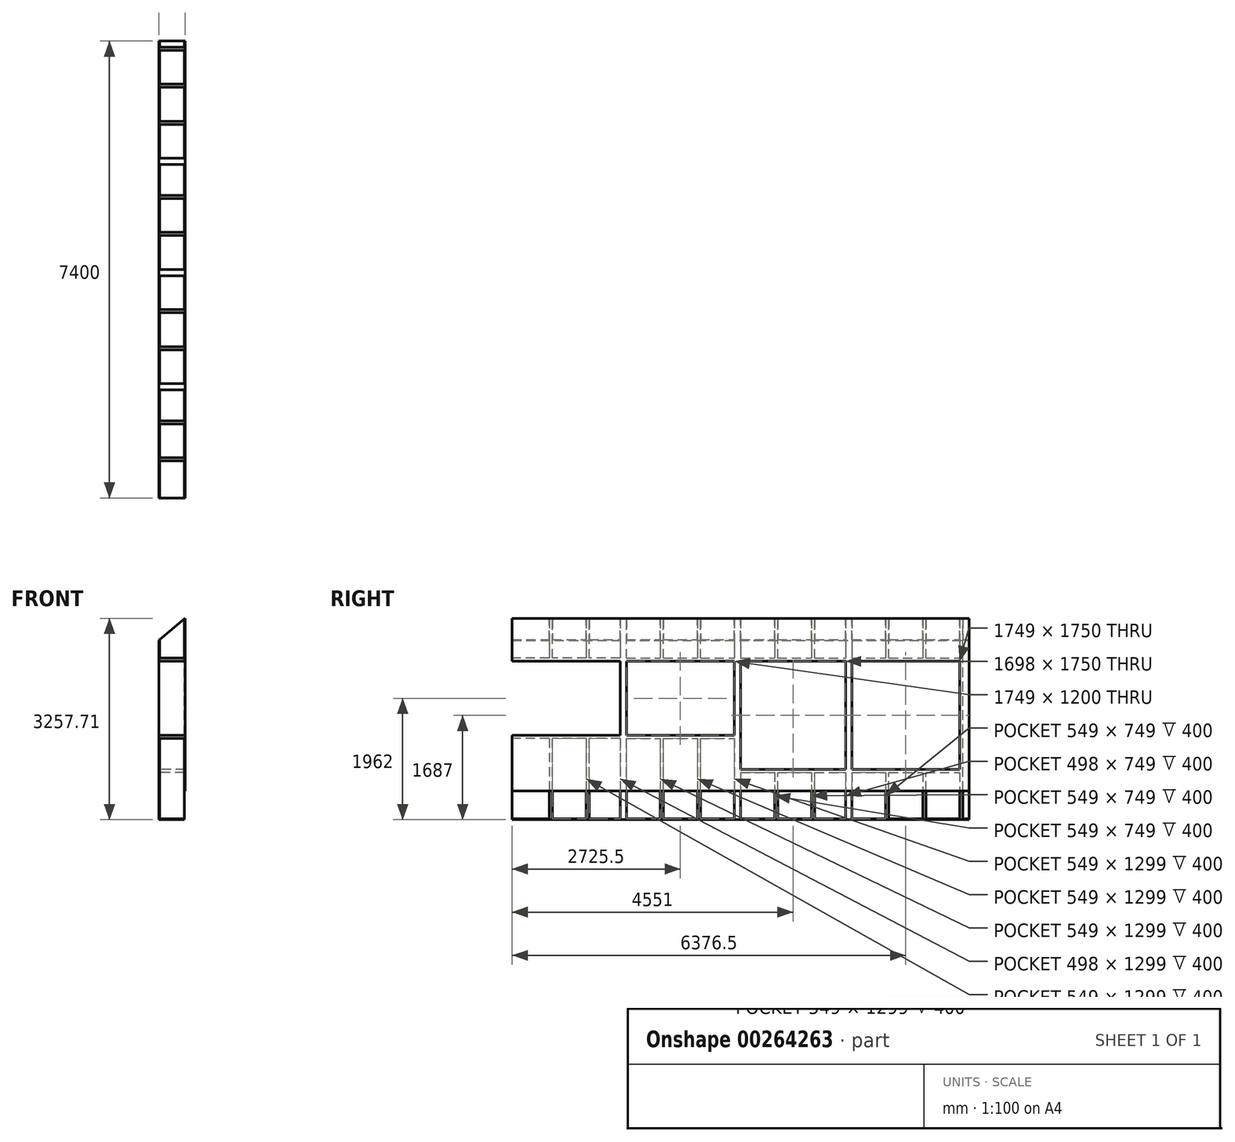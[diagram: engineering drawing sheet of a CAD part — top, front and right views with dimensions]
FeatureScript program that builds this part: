
annotation { "Feature Type Name" : "Feature", "Feature Type Description" : "" }
export const myFeature = defineFeature(function(context is Context, id is Id, definition is map)
    precondition{}
    {
        {
            var Q0;
            Q0=qCreatedBy(makeId("Right.planeOp"),FACE);
            var sketch = newSketch(context, id + "F0", { "sketchPlane" : qUnion([Q0])});
            skLineSegment(sketch, "E0.bottom", {"start": v(0, 0) * mm, "end": v(-7400, 0) * mm});
            skLineSegment(sketch, "E0.top", {"start": v(0, 3300) * mm, "end": v(-7400, 3300) * mm});
            skLineSegment(sketch, "E0.left", {"start": v(0, 0) * mm, "end": v(0, 3300) * mm});
            skLineSegment(sketch, "E0.right", {"start": v(-7400, 0) * mm, "end": v(-7400, 3300) * mm});
            skLineSegment(sketch, "E1", {"start": v(-6800, 3300) * mm, "end": v(-6800, 2601) * mm});
            skLineSegment(sketch, "E2", {"start": v(-6749, 0) * mm, "end": v(-6749, 1299) * mm});
            skLineSegment(sketch, "E3.1.0.0", {"start": v(-6149, 0) * mm, "end": v(-6149, 1299) * mm});
            skLineSegment(sketch, "E3.1.0.1", {"start": v(-6200, 3300) * mm, "end": v(-6200, 2601) * mm});
            skLineSegment(sketch, "E3.2.0.0", {"start": v(-5549, 0) * mm, "end": v(-5549, 3300) * mm});
            skLineSegment(sketch, "E3.2.0.1", {"start": v(-5600, 3300) * mm, "end": v(-5600, 0) * mm});
            skLineSegment(sketch, "E3.3.0.0", {"start": v(-4949, 0) * mm, "end": v(-4949, 1299) * mm});
            skLineSegment(sketch, "E3.3.0.1", {"start": v(-5000, 3300) * mm, "end": v(-5000, 2601) * mm});
            skLineSegment(sketch, "E3.4.0.0", {"start": v(-4349, 0) * mm, "end": v(-4349, 1299) * mm});
            skLineSegment(sketch, "E3.4.0.1", {"start": v(-4400, 3300) * mm, "end": v(-4400, 2601) * mm});
            skLineSegment(sketch, "E3.5.0.0", {"start": v(-3749, 0) * mm, "end": v(-3749, 3300) * mm});
            skLineSegment(sketch, "E3.5.0.1", {"start": v(-3800, 3300) * mm, "end": v(-3800, 0) * mm});
            skLineSegment(sketch, "E3.6.0.0", {"start": v(-3098, 0) * mm, "end": v(-3098, 749) * mm});
            skLineSegment(sketch, "E3.6.0.1", {"start": v(-3149, 3300) * mm, "end": v(-3149, 2601) * mm});
            skLineSegment(sketch, "E3.7.0.0", {"start": v(-2498, 0) * mm, "end": v(-2498, 749) * mm});
            skLineSegment(sketch, "E3.7.0.1", {"start": v(-2549, 3300) * mm, "end": v(-2549, 2601) * mm});
            skLineSegment(sketch, "E3.8.0.0", {"start": v(-1949, 0) * mm, "end": v(-1949, 3300) * mm});
            skLineSegment(sketch, "E3.8.0.1", {"start": v(-2000, 3300) * mm, "end": v(-2000, 0) * mm});
            skLineSegment(sketch, "E3.9.0.0", {"start": v(-1298, 0) * mm, "end": v(-1298, 749) * mm});
            skLineSegment(sketch, "E3.9.0.1", {"start": v(-1349, 3300) * mm, "end": v(-1349, 2601) * mm});
            skLineSegment(sketch, "E3.10.0.0", {"start": v(-698, 0) * mm, "end": v(-698, 749) * mm});
            skLineSegment(sketch, "E3.10.0.1", {"start": v(-749, 3300) * mm, "end": v(-749, 2601) * mm});
            skLineSegment(sketch, "E3.11.0.0", {"start": v(-98, 0) * mm, "end": v(-98, 3300) * mm});
            skLineSegment(sketch, "E3.11.0.1", {"start": v(-149, 3300) * mm, "end": v(-149, 0) * mm});
            skLineSegment(sketch, "E3.direction1", {"start": v(-6800, 0) * mm, "end": v(-6200, 0) * mm, "construction": true});
            skLineSegment(sketch, "E4", {"start": v(-7400, 1350) * mm, "end": v(-5651, 1350) * mm});
            skLineSegment(sketch, "E5", {"start": v(-5651, 3300) * mm, "end": v(-5651, 0) * mm});
            skLineSegment(sketch, "E6", {"start": v(-7400, 2550) * mm, "end": v(-5651, 2550) * mm});
            skLineSegment(sketch, "E7", {"start": v(-5651, 2601) * mm, "end": v(-7400, 2601) * mm});
            skLineSegment(sketch, "E8", {"start": v(-5651, 1299) * mm, "end": v(-7400, 1299) * mm});
            skLineSegment(sketch, "E9", {"start": v(-5549, 2601) * mm, "end": v(-3800, 2601) * mm});
            skLineSegment(sketch, "E10", {"start": v(-5549, 2550) * mm, "end": v(-3800, 2550) * mm});
            skLineSegment(sketch, "E11", {"start": v(-5549, 1350) * mm, "end": v(-3800, 1350) * mm});
            skLineSegment(sketch, "E12", {"start": v(-5549, 1299) * mm, "end": v(-3800, 1299) * mm});
            skLineSegment(sketch, "E13", {"start": v(-3698, 3300) * mm, "end": v(-3698, 0) * mm});
            skLineSegment(sketch, "E14.trimOffspring", {"start": v(-4349, 2601) * mm, "end": v(-4349, 3300) * mm});
            skLineSegment(sketch, "E15.trimOffspring", {"start": v(-4400, 1299) * mm, "end": v(-4400, 0) * mm});
            skLineSegment(sketch, "E16.trimOffspring", {"start": v(-4949, 2601) * mm, "end": v(-4949, 3300) * mm});
            skLineSegment(sketch, "E17.trimOffspring", {"start": v(-5000, 1299) * mm, "end": v(-5000, 0) * mm});
            skLineSegment(sketch, "E18.trimOffspring", {"start": v(-6149, 2601) * mm, "end": v(-6149, 3300) * mm});
            skLineSegment(sketch, "E19.trimOffspring", {"start": v(-6200, 1299) * mm, "end": v(-6200, 0) * mm});
            skLineSegment(sketch, "E20.trimOffspring", {"start": v(-6749, 2601) * mm, "end": v(-6749, 3300) * mm});
            skLineSegment(sketch, "E21.trimOffspring", {"start": v(-6800, 1299) * mm, "end": v(-6800, 0) * mm});
            skLineSegment(sketch, "E22", {"start": v(-3698, 2601) * mm, "end": v(-2000, 2601) * mm});
            skLineSegment(sketch, "E23", {"start": v(-3698, 2550) * mm, "end": v(-2000, 2550) * mm});
            skLineSegment(sketch, "E24", {"start": v(-3698, 749) * mm, "end": v(-2000, 749) * mm});
            skLineSegment(sketch, "E25", {"start": v(-3698, 800) * mm, "end": v(-2000, 800) * mm});
            skLineSegment(sketch, "E26.trimOffspring", {"start": v(-3149, 749) * mm, "end": v(-3149, 0) * mm});
            skLineSegment(sketch, "E27.trimOffspring", {"start": v(-3098, 2601) * mm, "end": v(-3098, 3300) * mm});
            skLineSegment(sketch, "E28.trimOffspring", {"start": v(-2549, 749) * mm, "end": v(-2549, 0) * mm});
            skLineSegment(sketch, "E29.trimOffspring", {"start": v(-2498, 2601) * mm, "end": v(-2498, 3300) * mm});
            skLineSegment(sketch, "E30", {"start": v(-1898, 3300) * mm, "end": v(-1898, 0) * mm});
            skLineSegment(sketch, "E31", {"start": v(-1898, 2601) * mm, "end": v(-149, 2601) * mm});
            skLineSegment(sketch, "E32", {"start": v(-1898, 2550) * mm, "end": v(-149, 2550) * mm});
            skLineSegment(sketch, "E33", {"start": v(-1898, 800) * mm, "end": v(-149, 800) * mm});
            skLineSegment(sketch, "E34", {"start": v(-1898, 749) * mm, "end": v(-149, 749) * mm});
            skLineSegment(sketch, "E35.trimOffspring", {"start": v(-1349, 749) * mm, "end": v(-1349, 0) * mm});
            skLineSegment(sketch, "E36.trimOffspring", {"start": v(-1298, 2601) * mm, "end": v(-1298, 3300) * mm});
            skLineSegment(sketch, "E37.trimOffspring", {"start": v(-749, 749) * mm, "end": v(-749, 0) * mm});
            skLineSegment(sketch, "E38.trimOffspring", {"start": v(-698, 2601) * mm, "end": v(-698, 3300) * mm});
            skSolve(sketch);
        }
        {
            var Q0;
            {var subQ0=sQuery(id+"F0.wireOp",EDGE,"E3.11.0.0");Q0=makeQuery(id+"F0.imprint","IMPRINT",FACE,{"disambiguationData":[TD([[makeQuery(id+"F0.imprint","IMPRINT",EDGE,{"derivedFrom":subQ0}),1.0]])]});}
            var Q1;
            {var subQ0=sQuery(id+"F0.wireOp",EDGE,"E3.9.0.0");Q1=makeQuery(id+"F0.imprint","IMPRINT",FACE,{"disambiguationData":[TD([[makeQuery(id+"F0.imprint","IMPRINT",EDGE,{"derivedFrom":subQ0}),1.0]])]});}
            var Q2;
            {var subQ0=sQuery(id+"F0.wireOp",EDGE,"E3.7.0.0");Q2=makeQuery(id+"F0.imprint","IMPRINT",FACE,{"disambiguationData":[TD([[makeQuery(id+"F0.imprint","IMPRINT",EDGE,{"derivedFrom":subQ0}),1.0]])]});}
            var Q3;
            {var subQ0=sQuery(id+"F0.wireOp",EDGE,"E3.6.0.0");Q3=makeQuery(id+"F0.imprint","IMPRINT",FACE,{"disambiguationData":[TD([[makeQuery(id+"F0.imprint","IMPRINT",EDGE,{"derivedFrom":subQ0}),1.0]])]});}
            var Q4;
            {var subQ0=sQuery(id+"F0.wireOp",EDGE,"E3.4.0.0");Q4=makeQuery(id+"F0.imprint","IMPRINT",FACE,{"disambiguationData":[TD([[makeQuery(id+"F0.imprint","IMPRINT",EDGE,{"derivedFrom":subQ0}),1.0]])]});}
            var Q5;
            {var subQ0=sQuery(id+"F0.wireOp",EDGE,"E3.3.0.0");Q5=makeQuery(id+"F0.imprint","IMPRINT",FACE,{"disambiguationData":[TD([[makeQuery(id+"F0.imprint","IMPRINT",EDGE,{"derivedFrom":subQ0}),1.0]])]});}
            var Q6;
            {var subQ0=sQuery(id+"F0.wireOp",EDGE,"E3.1.0.0");Q6=makeQuery(id+"F0.imprint","IMPRINT",FACE,{"disambiguationData":[TD([[makeQuery(id+"F0.imprint","IMPRINT",EDGE,{"derivedFrom":subQ0}),1.0]])]});}
            var Q7;
            {var subQ0=sQuery(id+"F0.wireOp",EDGE,"E2");Q7=makeQuery(id+"F0.imprint","IMPRINT",FACE,{"disambiguationData":[TD([[makeQuery(id+"F0.imprint","IMPRINT",EDGE,{"derivedFrom":subQ0}),1.0]])]});}
            var Q8;
            {var subQ0=sQuery(id+"F0.wireOp",EDGE,"E3.9.0.1");Q8=makeQuery(id+"F0.imprint","IMPRINT",FACE,{"disambiguationData":[TD([[makeQuery(id+"F0.imprint","IMPRINT",EDGE,{"derivedFrom":subQ0}),1.0]])]});}
            var Q9;
            {var subQ0=sQuery(id+"F0.wireOp",EDGE,"E3.7.0.1");Q9=makeQuery(id+"F0.imprint","IMPRINT",FACE,{"disambiguationData":[TD([[makeQuery(id+"F0.imprint","IMPRINT",EDGE,{"derivedFrom":subQ0}),1.0]])]});}
            var Q10;
            {var subQ0=sQuery(id+"F0.wireOp",EDGE,"E3.6.0.1");Q10=makeQuery(id+"F0.imprint","IMPRINT",FACE,{"disambiguationData":[TD([[makeQuery(id+"F0.imprint","IMPRINT",EDGE,{"derivedFrom":subQ0}),1.0]])]});}
            var Q11;
            {var subQ0=sQuery(id+"F0.wireOp",EDGE,"E3.4.0.1");Q11=makeQuery(id+"F0.imprint","IMPRINT",FACE,{"disambiguationData":[TD([[makeQuery(id+"F0.imprint","IMPRINT",EDGE,{"derivedFrom":subQ0}),1.0]])]});}
            var Q12;
            {var subQ0=sQuery(id+"F0.wireOp",EDGE,"E3.3.0.1");Q12=makeQuery(id+"F0.imprint","IMPRINT",FACE,{"disambiguationData":[TD([[makeQuery(id+"F0.imprint","IMPRINT",EDGE,{"derivedFrom":subQ0}),1.0]])]});}
            var Q13;
            {var subQ0=sQuery(id+"F0.wireOp",EDGE,"E3.1.0.1");Q13=makeQuery(id+"F0.imprint","IMPRINT",FACE,{"disambiguationData":[TD([[makeQuery(id+"F0.imprint","IMPRINT",EDGE,{"derivedFrom":subQ0}),1.0]])]});}
            var Q14;
            {var subQ0=sQuery(id+"F0.wireOp",EDGE,"E1");Q14=makeQuery(id+"F0.imprint","IMPRINT",FACE,{"disambiguationData":[TD([[makeQuery(id+"F0.imprint","IMPRINT",EDGE,{"derivedFrom":subQ0}),1.0]])]});}
            var Q15;
            {var subQ4=sQuery(id+"F0.wireOp",EDGE,"E3.10.0.0");Q15=makeQuery(id+"F0.imprint","IMPRINT",FACE,{"disambiguationData":[TD([[makeQuery(id+"F0.imprint","IMPRINT",EDGE,{"derivedFrom":subQ4}),1.0]])]});}
            var Q16;
            {var subQ0=sQuery(id+"F0.wireOp",EDGE,"E3.8.0.0");Q16=makeQuery(id+"F0.imprint","IMPRINT",FACE,{"disambiguationData":[TD([[makeQuery(id+"F0.imprint","IMPRINT",EDGE,{"derivedFrom":subQ0}),-1.0]])]});}
            var Q17;
            {var subQ4=sQuery(id+"F0.wireOp",EDGE,"E3.8.0.0");Q17=makeQuery(id+"F0.imprint","IMPRINT",FACE,{"disambiguationData":[TD([[makeQuery(id+"F0.imprint","IMPRINT",EDGE,{"derivedFrom":subQ4}),1.0]])]});}
            var Q18;
            {var subQ4=sQuery(id+"F0.wireOp",EDGE,"E3.5.0.0");Q18=makeQuery(id+"F0.imprint","IMPRINT",FACE,{"disambiguationData":[TD([[makeQuery(id+"F0.imprint","IMPRINT",EDGE,{"derivedFrom":subQ4}),-1.0]])]});}
            var Q19;
            {var subQ4=sQuery(id+"F0.wireOp",EDGE,"E3.5.0.0");Q19=makeQuery(id+"F0.imprint","IMPRINT",FACE,{"disambiguationData":[TD([[makeQuery(id+"F0.imprint","IMPRINT",EDGE,{"derivedFrom":subQ4}),1.0]])]});}
            var Q20;
            {var subQ5=sQuery(id+"F0.wireOp",EDGE,"E3.2.0.1");Q20=makeQuery(id+"F0.imprint","IMPRINT",FACE,{"disambiguationData":[TD([[makeQuery(id+"F0.imprint","IMPRINT",EDGE,{"derivedFrom":subQ5}),1.0]])]});}
            var Q21;
            {var subQ4=sQuery(id+"F0.wireOp",EDGE,"E3.2.0.1");Q21=makeQuery(id+"F0.imprint","IMPRINT",FACE,{"disambiguationData":[TD([[makeQuery(id+"F0.imprint","IMPRINT",EDGE,{"derivedFrom":subQ4}),-1.0]])]});}
            var Q22;
            {var subQ4=sQuery(id+"F0.wireOp",EDGE,"E4");Q22=makeQuery(id+"F0.imprint","IMPRINT",FACE,{"disambiguationData":[TD([[makeQuery(id+"F0.imprint","IMPRINT",EDGE,{"derivedFrom":subQ4}),-1.0]])]});}
            var Q23;
            {var subQ0=sQuery(id+"F0.wireOp",EDGE,"E6");Q23=makeQuery(id+"F0.imprint","IMPRINT",FACE,{"disambiguationData":[TD([[makeQuery(id+"F0.imprint","IMPRINT",EDGE,{"derivedFrom":subQ0}),1.0]])]});}
            var Q24;
            {var subQ4=sQuery(id+"F0.wireOp",EDGE,"E33");Q24=makeQuery(id+"F0.imprint","IMPRINT",FACE,{"disambiguationData":[TD([[makeQuery(id+"F0.imprint","IMPRINT",EDGE,{"derivedFrom":subQ4}),-1.0]])]});}
            var Q25;
            {var subQ5=sQuery(id+"F0.wireOp",EDGE,"E25");Q25=makeQuery(id+"F0.imprint","IMPRINT",FACE,{"disambiguationData":[TD([[makeQuery(id+"F0.imprint","IMPRINT",EDGE,{"derivedFrom":subQ5}),-1.0]])]});}
            var Q26;
            {var subQ4=sQuery(id+"F0.wireOp",EDGE,"E11");Q26=makeQuery(id+"F0.imprint","IMPRINT",FACE,{"disambiguationData":[TD([[makeQuery(id+"F0.imprint","IMPRINT",EDGE,{"derivedFrom":subQ4}),-1.0]])]});}
            var Q27;
            {var subQ5=sQuery(id+"F0.wireOp",EDGE,"E10");Q27=makeQuery(id+"F0.imprint","IMPRINT",FACE,{"disambiguationData":[TD([[makeQuery(id+"F0.imprint","IMPRINT",EDGE,{"derivedFrom":subQ5}),1.0]])]});}
            var Q28;
            {var subQ5=sQuery(id+"F0.wireOp",EDGE,"E32");Q28=makeQuery(id+"F0.imprint","IMPRINT",FACE,{"disambiguationData":[TD([[makeQuery(id+"F0.imprint","IMPRINT",EDGE,{"derivedFrom":subQ5}),1.0]])]});}
            var Q29;
            {var subQ5=sQuery(id+"F0.wireOp",EDGE,"E23");Q29=makeQuery(id+"F0.imprint","IMPRINT",FACE,{"disambiguationData":[TD([[makeQuery(id+"F0.imprint","IMPRINT",EDGE,{"derivedFrom":subQ5}),1.0]])]});}
            var Q30;
            {var subQ0=sQuery(id+"F0.wireOp",EDGE,"E3.10.0.1");Q30=makeQuery(id+"F0.imprint","IMPRINT",FACE,{"disambiguationData":[TD([[makeQuery(id+"F0.imprint","IMPRINT",EDGE,{"derivedFrom":subQ0}),1.0]])]});}
            extrude(context, id + "F1", {"entities" : qUnion([Q0, Q1, Q2, Q3, Q4, Q5, Q6, Q7, Q8, Q9, Q10, Q11, Q12, Q13, Q14, Q15, Q16, Q17, Q18, Q19, Q20, Q21, Q22, Q23, Q24, Q25, Q26, Q27, Q28, Q29, Q30]), "depth" : 400 * mm});
        }
        {
            var Q0;
            Q0=makeQuery(id+"F1.opExtrude","CAP_FACE",FACE,{"disambiguationData":[OSD([sQuery(id+"F0.wireOp",EDGE,"E0.bottom"),sQuery(id+"F0.wireOp",EDGE,"E0.top"),sQuery(id+"F0.wireOp",EDGE,"E0.right"),sQuery(id+"F0.wireOp",EDGE,"E1"),sQuery(id+"F0.wireOp",EDGE,"E2"),sQuery(id+"F0.wireOp",EDGE,"E3.1.0.0"),sQuery(id+"F0.wireOp",EDGE,"E3.1.0.1"),sQuery(id+"F0.wireOp",EDGE,"E3.2.0.0"),sQuery(id+"F0.wireOp",EDGE,"E3.3.0.0"),sQuery(id+"F0.wireOp",EDGE,"E3.3.0.1"),sQuery(id+"F0.wireOp",EDGE,"E3.4.0.0"),sQuery(id+"F0.wireOp",EDGE,"E3.4.0.1"),sQuery(id+"F0.wireOp",EDGE,"E3.5.0.1"),sQuery(id+"F0.wireOp",EDGE,"E3.6.0.0"),sQuery(id+"F0.wireOp",EDGE,"E3.6.0.1"),sQuery(id+"F0.wireOp",EDGE,"E3.7.0.0"),sQuery(id+"F0.wireOp",EDGE,"E3.7.0.1"),sQuery(id+"F0.wireOp",EDGE,"E3.8.0.1"),sQuery(id+"F0.wireOp",EDGE,"E3.9.0.0"),sQuery(id+"F0.wireOp",EDGE,"E3.9.0.1"),sQuery(id+"F0.wireOp",EDGE,"E3.10.0.0"),sQuery(id+"F0.wireOp",EDGE,"E3.10.0.1"),sQuery(id+"F0.wireOp",EDGE,"E4"),sQuery(id+"F0.wireOp",EDGE,"E5"),sQuery(id+"F0.wireOp",EDGE,"E6"),sQuery(id+"F0.wireOp",EDGE,"E7"),sQuery(id+"F0.wireOp",EDGE,"E8"),sQuery(id+"F0.wireOp",EDGE,"E9"),sQuery(id+"F0.wireOp",EDGE,"E10"),sQuery(id+"F0.wireOp",EDGE,"E11"),sQuery(id+"F0.wireOp",EDGE,"E12"),sQuery(id+"F0.wireOp",EDGE,"E13"),sQuery(id+"F0.wireOp",EDGE,"E14.trimOffspring"),sQuery(id+"F0.wireOp",EDGE,"E15.trimOffspring"),sQuery(id+"F0.wireOp",EDGE,"E16.trimOffspring"),sQuery(id+"F0.wireOp",EDGE,"E17.trimOffspring"),sQuery(id+"F0.wireOp",EDGE,"E18.trimOffspring"),sQuery(id+"F0.wireOp",EDGE,"E19.trimOffspring"),sQuery(id+"F0.wireOp",EDGE,"E20.trimOffspring"),sQuery(id+"F0.wireOp",EDGE,"E21.trimOffspring"),sQuery(id+"F0.wireOp",EDGE,"E22"),sQuery(id+"F0.wireOp",EDGE,"E23"),sQuery(id+"F0.wireOp",EDGE,"E24"),sQuery(id+"F0.wireOp",EDGE,"E25"),sQuery(id+"F0.wireOp",EDGE,"E26.trimOffspring"),sQuery(id+"F0.wireOp",EDGE,"E27.trimOffspring"),sQuery(id+"F0.wireOp",EDGE,"E28.trimOffspring"),sQuery(id+"F0.wireOp",EDGE,"E29.trimOffspring"),sQuery(id+"F0.wireOp",EDGE,"E30"),sQuery(id+"F0.wireOp",EDGE,"E31"),sQuery(id+"F0.wireOp",EDGE,"E32"),sQuery(id+"F0.wireOp",EDGE,"E33"),sQuery(id+"F0.wireOp",EDGE,"E34"),sQuery(id+"F0.wireOp",EDGE,"E35.trimOffspring"),sQuery(id+"F0.wireOp",EDGE,"E36.trimOffspring")])],"isStart":true});
            var sketch = newSketch(context, id + "F2", { "sketchPlane" : qUnion([Q0])});
            skLineSegment(sketch, "E39.bottom", {"start": v(0, 0) * mm, "end": v(7400, 0) * mm});
            skLineSegment(sketch, "E39.top", {"start": v(0, 3200) * mm, "end": v(7400, 3200) * mm});
            skLineSegment(sketch, "E39.left", {"start": v(0, 0) * mm, "end": v(0, 3200) * mm});
            skLineSegment(sketch, "E39.right", {"start": v(7400, 0) * mm, "end": v(7400, 3200) * mm});
            skLineSegment(sketch, "E40.bottom", {"start": v(2000, 2550) * mm, "end": v(3698, 2550) * mm});
            skLineSegment(sketch, "E40.top", {"start": v(2000, 800) * mm, "end": v(3698, 800) * mm});
            skLineSegment(sketch, "E40.left", {"start": v(2000, 2550) * mm, "end": v(2000, 800) * mm});
            skLineSegment(sketch, "E40.right", {"start": v(3698, 2550) * mm, "end": v(3698, 800) * mm});
            skLineSegment(sketch, "E41.bottom", {"start": v(3800, 2550) * mm, "end": v(5549, 2550) * mm});
            skLineSegment(sketch, "E41.top", {"start": v(3800, 1350) * mm, "end": v(5549, 1350) * mm});
            skLineSegment(sketch, "E41.left", {"start": v(3800, 2550) * mm, "end": v(3800, 1350) * mm});
            skLineSegment(sketch, "E41.right", {"start": v(5549, 2550) * mm, "end": v(5549, 1350) * mm});
            skLineSegment(sketch, "E42.bottom", {"start": v(5651, 2550) * mm, "end": v(7400, 2550) * mm});
            skLineSegment(sketch, "E42.top", {"start": v(5651, 1350) * mm, "end": v(7400, 1350) * mm});
            skLineSegment(sketch, "E42.left", {"start": v(5651, 2550) * mm, "end": v(5651, 1350) * mm});
            skLineSegment(sketch, "E42.right", {"start": v(7400, 2550) * mm, "end": v(7400, 1350) * mm});
            skLineSegment(sketch, "E43.bottom", {"start": v(149, 2550) * mm, "end": v(1898, 2550) * mm});
            skLineSegment(sketch, "E43.top", {"start": v(149, 800) * mm, "end": v(1898, 800) * mm});
            skLineSegment(sketch, "E43.left", {"start": v(149, 2550) * mm, "end": v(149, 800) * mm});
            skLineSegment(sketch, "E43.right", {"start": v(1898, 2550) * mm, "end": v(1898, 800) * mm});
            skSolve(sketch);
        }
        {
            var Q0;
            {var subQ2=sQuery(id+"F2.wireOp",EDGE,"E39.left");Q0=makeQuery(id+"F2.imprint","IMPRINT",FACE,{"disambiguationData":[TD([[makeQuery(id+"F2.imprint","IMPRINT",EDGE,{"derivedFrom":subQ2}),-1.0]])]});}
            var Q1;
            {var subQ1=sQuery(id+"F0.wireOp",EDGE,"E3.9.0.0");var subQ2=makeQuery(id+"F1.opExtrude","CAP_EDGE",EDGE,{"disambiguationData":[OSD([subQ1])],"isStart":true});Q1=makeQuery(id+"F2.imprint","IMPRINT",FACE,{"disambiguationData":[TD([[makeQuery(id+"F2.imprint","IMPRINT",EDGE,{"derivedFrom":subQ2}),1.0]])]});}
            var Q2;
            {var subQ5=sQuery(id+"F0.wireOp",EDGE,"E35.trimOffspring");var subQ6=makeQuery(id+"F1.opExtrude","CAP_EDGE",EDGE,{"disambiguationData":[OSD([subQ5])],"isStart":true});Q2=makeQuery(id+"F2.imprint","IMPRINT",FACE,{"disambiguationData":[TD([[makeQuery(id+"F2.imprint","IMPRINT",EDGE,{"derivedFrom":subQ6}),1.0]])]});}
            var Q3;
            {var subQ1=sQuery(id+"F0.wireOp",EDGE,"E3.7.0.0");var subQ2=makeQuery(id+"F1.opExtrude","CAP_EDGE",EDGE,{"disambiguationData":[OSD([subQ1])],"isStart":true});Q3=makeQuery(id+"F2.imprint","IMPRINT",FACE,{"disambiguationData":[TD([[makeQuery(id+"F2.imprint","IMPRINT",EDGE,{"derivedFrom":subQ2}),1.0]])]});}
            var Q4;
            {var subQ1=sQuery(id+"F0.wireOp",EDGE,"E3.6.0.0");var subQ2=makeQuery(id+"F1.opExtrude","CAP_EDGE",EDGE,{"disambiguationData":[OSD([subQ1])],"isStart":true});Q4=makeQuery(id+"F2.imprint","IMPRINT",FACE,{"disambiguationData":[TD([[makeQuery(id+"F2.imprint","IMPRINT",EDGE,{"derivedFrom":subQ2}),1.0]])]});}
            var Q5;
            {var subQ5=sQuery(id+"F0.wireOp",EDGE,"E26.trimOffspring");var subQ6=makeQuery(id+"F1.opExtrude","CAP_EDGE",EDGE,{"disambiguationData":[OSD([subQ5])],"isStart":true});Q5=makeQuery(id+"F2.imprint","IMPRINT",FACE,{"disambiguationData":[TD([[makeQuery(id+"F2.imprint","IMPRINT",EDGE,{"derivedFrom":subQ6}),1.0]])]});}
            var Q6;
            {var subQ1=sQuery(id+"F0.wireOp",EDGE,"E3.4.0.0");var subQ2=makeQuery(id+"F1.opExtrude","CAP_EDGE",EDGE,{"disambiguationData":[OSD([subQ1])],"isStart":true});Q6=makeQuery(id+"F2.imprint","IMPRINT",FACE,{"disambiguationData":[TD([[makeQuery(id+"F2.imprint","IMPRINT",EDGE,{"derivedFrom":subQ2}),1.0]])]});}
            var Q7;
            {var subQ1=sQuery(id+"F0.wireOp",EDGE,"E3.3.0.0");var subQ2=makeQuery(id+"F1.opExtrude","CAP_EDGE",EDGE,{"disambiguationData":[OSD([subQ1])],"isStart":true});Q7=makeQuery(id+"F2.imprint","IMPRINT",FACE,{"disambiguationData":[TD([[makeQuery(id+"F2.imprint","IMPRINT",EDGE,{"derivedFrom":subQ2}),1.0]])]});}
            var Q8;
            {var subQ5=sQuery(id+"F0.wireOp",EDGE,"E17.trimOffspring");var subQ6=makeQuery(id+"F1.opExtrude","CAP_EDGE",EDGE,{"disambiguationData":[OSD([subQ5])],"isStart":true});Q8=makeQuery(id+"F2.imprint","IMPRINT",FACE,{"disambiguationData":[TD([[makeQuery(id+"F2.imprint","IMPRINT",EDGE,{"derivedFrom":subQ6}),1.0]])]});}
            var Q9;
            {var subQ1=sQuery(id+"F0.wireOp",EDGE,"E3.1.0.0");var subQ2=makeQuery(id+"F1.opExtrude","CAP_EDGE",EDGE,{"disambiguationData":[OSD([subQ1])],"isStart":true});Q9=makeQuery(id+"F2.imprint","IMPRINT",FACE,{"disambiguationData":[TD([[makeQuery(id+"F2.imprint","IMPRINT",EDGE,{"derivedFrom":subQ2}),1.0]])]});}
            var Q10;
            {var subQ1=sQuery(id+"F0.wireOp",EDGE,"E2");var subQ2=makeQuery(id+"F1.opExtrude","CAP_EDGE",EDGE,{"disambiguationData":[OSD([subQ1])],"isStart":true});Q10=makeQuery(id+"F2.imprint","IMPRINT",FACE,{"disambiguationData":[TD([[makeQuery(id+"F2.imprint","IMPRINT",EDGE,{"derivedFrom":subQ2}),1.0]])]});}
            var Q11;
            {var subQ1=sQuery(id+"F0.wireOp",EDGE,"E21.trimOffspring");var subQ2=makeQuery(id+"F1.opExtrude","CAP_EDGE",EDGE,{"disambiguationData":[OSD([subQ1])],"isStart":true});Q11=makeQuery(id+"F2.imprint","IMPRINT",FACE,{"disambiguationData":[TD([[makeQuery(id+"F2.imprint","IMPRINT",EDGE,{"derivedFrom":subQ2}),1.0]])]});}
            var Q12;
            {var subQ5=sQuery(id+"F0.wireOp",EDGE,"E36.trimOffspring");var subQ6=makeQuery(id+"F1.opExtrude","CAP_EDGE",EDGE,{"disambiguationData":[OSD([subQ5])],"isStart":true});Q12=makeQuery(id+"F2.imprint","IMPRINT",FACE,{"disambiguationData":[TD([[makeQuery(id+"F2.imprint","IMPRINT",EDGE,{"derivedFrom":subQ6}),1.0]])]});}
            var Q13;
            {var subQ1=sQuery(id+"F0.wireOp",EDGE,"E3.9.0.1");var subQ2=makeQuery(id+"F1.opExtrude","CAP_EDGE",EDGE,{"disambiguationData":[OSD([subQ1])],"isStart":true});Q13=makeQuery(id+"F2.imprint","IMPRINT",FACE,{"disambiguationData":[TD([[makeQuery(id+"F2.imprint","IMPRINT",EDGE,{"derivedFrom":subQ2}),1.0]])]});}
            var Q14;
            {var subQ5=sQuery(id+"F0.wireOp",EDGE,"E29.trimOffspring");var subQ6=makeQuery(id+"F1.opExtrude","CAP_EDGE",EDGE,{"disambiguationData":[OSD([subQ5])],"isStart":true});Q14=makeQuery(id+"F2.imprint","IMPRINT",FACE,{"disambiguationData":[TD([[makeQuery(id+"F2.imprint","IMPRINT",EDGE,{"derivedFrom":subQ6}),1.0]])]});}
            var Q15;
            {var subQ1=sQuery(id+"F0.wireOp",EDGE,"E3.7.0.1");var subQ2=makeQuery(id+"F1.opExtrude","CAP_EDGE",EDGE,{"disambiguationData":[OSD([subQ1])],"isStart":true});Q15=makeQuery(id+"F2.imprint","IMPRINT",FACE,{"disambiguationData":[TD([[makeQuery(id+"F2.imprint","IMPRINT",EDGE,{"derivedFrom":subQ2}),1.0]])]});}
            var Q16;
            {var subQ1=sQuery(id+"F0.wireOp",EDGE,"E3.6.0.1");var subQ2=makeQuery(id+"F1.opExtrude","CAP_EDGE",EDGE,{"disambiguationData":[OSD([subQ1])],"isStart":true});Q16=makeQuery(id+"F2.imprint","IMPRINT",FACE,{"disambiguationData":[TD([[makeQuery(id+"F2.imprint","IMPRINT",EDGE,{"derivedFrom":subQ2}),1.0]])]});}
            var Q17;
            {var subQ5=sQuery(id+"F0.wireOp",EDGE,"E14.trimOffspring");var subQ6=makeQuery(id+"F1.opExtrude","CAP_EDGE",EDGE,{"disambiguationData":[OSD([subQ5])],"isStart":true});Q17=makeQuery(id+"F2.imprint","IMPRINT",FACE,{"disambiguationData":[TD([[makeQuery(id+"F2.imprint","IMPRINT",EDGE,{"derivedFrom":subQ6}),1.0]])]});}
            var Q18;
            {var subQ1=sQuery(id+"F0.wireOp",EDGE,"E3.4.0.1");var subQ2=makeQuery(id+"F1.opExtrude","CAP_EDGE",EDGE,{"disambiguationData":[OSD([subQ1])],"isStart":true});Q18=makeQuery(id+"F2.imprint","IMPRINT",FACE,{"disambiguationData":[TD([[makeQuery(id+"F2.imprint","IMPRINT",EDGE,{"derivedFrom":subQ2}),1.0]])]});}
            var Q19;
            {var subQ5=sQuery(id+"F0.wireOp",EDGE,"E3.3.0.1");var subQ6=makeQuery(id+"F1.opExtrude","CAP_EDGE",EDGE,{"disambiguationData":[OSD([subQ5])],"isStart":true});Q19=makeQuery(id+"F2.imprint","IMPRINT",FACE,{"disambiguationData":[TD([[makeQuery(id+"F2.imprint","IMPRINT",EDGE,{"derivedFrom":subQ6}),1.0]])]});}
            var Q20;
            {var subQ5=sQuery(id+"F0.wireOp",EDGE,"E18.trimOffspring");var subQ6=makeQuery(id+"F1.opExtrude","CAP_EDGE",EDGE,{"disambiguationData":[OSD([subQ5])],"isStart":true});Q20=makeQuery(id+"F2.imprint","IMPRINT",FACE,{"disambiguationData":[TD([[makeQuery(id+"F2.imprint","IMPRINT",EDGE,{"derivedFrom":subQ6}),1.0]])]});}
            var Q21;
            {var subQ1=sQuery(id+"F0.wireOp",EDGE,"E3.1.0.1");var subQ2=makeQuery(id+"F1.opExtrude","CAP_EDGE",EDGE,{"disambiguationData":[OSD([subQ1])],"isStart":true});Q21=makeQuery(id+"F2.imprint","IMPRINT",FACE,{"disambiguationData":[TD([[makeQuery(id+"F2.imprint","IMPRINT",EDGE,{"derivedFrom":subQ2}),1.0]])]});}
            var Q22;
            {var subQ1=sQuery(id+"F0.wireOp",EDGE,"E1");var subQ2=makeQuery(id+"F1.opExtrude","CAP_EDGE",EDGE,{"disambiguationData":[OSD([subQ1])],"isStart":true});Q22=makeQuery(id+"F2.imprint","IMPRINT",FACE,{"disambiguationData":[TD([[makeQuery(id+"F2.imprint","IMPRINT",EDGE,{"derivedFrom":subQ2}),1.0]])]});}
            var Q23;
            Q23=makeQuery(id+"F2.imprint","IMPRINT",FACE,{"disambiguationData":[TD([[makeQuery(id+"F2.imprint","IMPRINT",EDGE,{"derivedFrom":sQuery(id+"F2.wireOp",EDGE,"4E25h8tN-b1jE-w8Na-nv1k-SOlIuhCm08Cw.bottom")}),-1.0]])]});
            var Q24;
            {var subQ1=sQuery(id+"F0.wireOp",EDGE,"E3.11.0.1");var subQ2=sQuery(id+"F0.wireOp",EDGE,"E31");var subQ3=makeQuery(id+"F0.imprint","INTERSECT",VERTEX,{"derivedFrom":[subQ1,subQ2]});var subQ9=makeQuery(id+"F1.opExtrude","CAP_EDGE",EDGE,{"disambiguationData":[OSD([subQ2]),TDD([makeQuery(id+"F0.imprint","IMPRINT",EDGE,{"disambiguationData":[TD([[subQ3,1.0]])],"derivedFrom":subQ2})])],"isStart":true});Q24=makeQuery(id+"F2.imprint","IMPRINT",FACE,{"disambiguationData":[TD([[makeQuery(id+"F2.imprint","IMPRINT",EDGE,{"derivedFrom":subQ9}),-1.0]])]});}
            var Q25;
            {var subQ1=sQuery(id+"F0.wireOp",EDGE,"E3.10.0.0");var subQ2=makeQuery(id+"F1.opExtrude","CAP_EDGE",EDGE,{"disambiguationData":[OSD([subQ1])],"isStart":true});Q25=makeQuery(id+"F2.imprint","IMPRINT",FACE,{"disambiguationData":[TD([[makeQuery(id+"F2.imprint","IMPRINT",EDGE,{"derivedFrom":subQ2}),1.0]])]});}
            var Q26;
            Q26=makeQuery(id+"F2.imprint","IMPRINT",FACE,{"disambiguationData":[TD([[makeQuery(id+"F2.imprint","IMPRINT",EDGE,{"derivedFrom":sQuery(id+"F2.wireOp",EDGE,"E40.bottom")}),-1.0]])]});
            extrude(context, id + "F3", {"entities" : qUnion([Q0, Q1, Q2, Q3, Q4, Q5, Q6, Q7, Q8, Q9, Q10, Q11, Q12, Q13, Q14, Q15, Q16, Q17, Q18, Q19, Q20, Q21, Q22, Q23, Q24, Q25, Q26]), "operationType" : NewBodyOperationType.ADD, "depth" : 12 * mm});
        }
        {
            var Q0;
            Q0=makeQuery(id+"F1.opExtrude","CAP_FACE",FACE,{"disambiguationData":[OSD([sQuery(id+"F0.wireOp",EDGE,"E0.bottom"),sQuery(id+"F0.wireOp",EDGE,"E0.top"),sQuery(id+"F0.wireOp",EDGE,"E0.right"),sQuery(id+"F0.wireOp",EDGE,"E1"),sQuery(id+"F0.wireOp",EDGE,"E2"),sQuery(id+"F0.wireOp",EDGE,"E3.1.0.0"),sQuery(id+"F0.wireOp",EDGE,"E3.1.0.1"),sQuery(id+"F0.wireOp",EDGE,"E3.2.0.0"),sQuery(id+"F0.wireOp",EDGE,"E3.3.0.0"),sQuery(id+"F0.wireOp",EDGE,"E3.3.0.1"),sQuery(id+"F0.wireOp",EDGE,"E3.4.0.0"),sQuery(id+"F0.wireOp",EDGE,"E3.4.0.1"),sQuery(id+"F0.wireOp",EDGE,"E3.5.0.1"),sQuery(id+"F0.wireOp",EDGE,"E3.6.0.0"),sQuery(id+"F0.wireOp",EDGE,"E3.6.0.1"),sQuery(id+"F0.wireOp",EDGE,"E3.7.0.0"),sQuery(id+"F0.wireOp",EDGE,"E3.7.0.1"),sQuery(id+"F0.wireOp",EDGE,"E3.8.0.1"),sQuery(id+"F0.wireOp",EDGE,"E3.9.0.0"),sQuery(id+"F0.wireOp",EDGE,"E3.9.0.1"),sQuery(id+"F0.wireOp",EDGE,"E3.10.0.0"),sQuery(id+"F0.wireOp",EDGE,"E3.10.0.1"),sQuery(id+"F0.wireOp",EDGE,"E4"),sQuery(id+"F0.wireOp",EDGE,"E5"),sQuery(id+"F0.wireOp",EDGE,"E6"),sQuery(id+"F0.wireOp",EDGE,"E7"),sQuery(id+"F0.wireOp",EDGE,"E8"),sQuery(id+"F0.wireOp",EDGE,"E9"),sQuery(id+"F0.wireOp",EDGE,"E10"),sQuery(id+"F0.wireOp",EDGE,"E11"),sQuery(id+"F0.wireOp",EDGE,"E12"),sQuery(id+"F0.wireOp",EDGE,"E13"),sQuery(id+"F0.wireOp",EDGE,"E14.trimOffspring"),sQuery(id+"F0.wireOp",EDGE,"E15.trimOffspring"),sQuery(id+"F0.wireOp",EDGE,"E16.trimOffspring"),sQuery(id+"F0.wireOp",EDGE,"E17.trimOffspring"),sQuery(id+"F0.wireOp",EDGE,"E18.trimOffspring"),sQuery(id+"F0.wireOp",EDGE,"E19.trimOffspring"),sQuery(id+"F0.wireOp",EDGE,"E20.trimOffspring"),sQuery(id+"F0.wireOp",EDGE,"E21.trimOffspring"),sQuery(id+"F0.wireOp",EDGE,"E22"),sQuery(id+"F0.wireOp",EDGE,"E23"),sQuery(id+"F0.wireOp",EDGE,"E24"),sQuery(id+"F0.wireOp",EDGE,"E25"),sQuery(id+"F0.wireOp",EDGE,"E26.trimOffspring"),sQuery(id+"F0.wireOp",EDGE,"E27.trimOffspring"),sQuery(id+"F0.wireOp",EDGE,"E28.trimOffspring"),sQuery(id+"F0.wireOp",EDGE,"E29.trimOffspring"),sQuery(id+"F0.wireOp",EDGE,"E30"),sQuery(id+"F0.wireOp",EDGE,"E31"),sQuery(id+"F0.wireOp",EDGE,"E32"),sQuery(id+"F0.wireOp",EDGE,"E33"),sQuery(id+"F0.wireOp",EDGE,"E34"),sQuery(id+"F0.wireOp",EDGE,"E35.trimOffspring"),sQuery(id+"F0.wireOp",EDGE,"E36.trimOffspring")])],"isStart":false});
            var sketch = newSketch(context, id + "F4", { "sketchPlane" : qUnion([Q0])});
            skLineSegment(sketch, "E44.bottom", {"start": v(0, 450) * mm, "end": v(-7400, 450) * mm});
            skLineSegment(sketch, "E44.top", {"start": v(0, 3300) * mm, "end": v(-7400, 3300) * mm});
            skLineSegment(sketch, "E44.left", {"start": v(0, 450) * mm, "end": v(0, 3300) * mm});
            skLineSegment(sketch, "E44.right", {"start": v(-7400, 450) * mm, "end": v(-7400, 3300) * mm});
            skSolve(sketch);
        }
        {
            var Q0;
            {var subQ5=sQuery(id+"F0.wireOp",EDGE,"E36.trimOffspring");var subQ6=makeQuery(id+"F1.opExtrude","CAP_EDGE",EDGE,{"disambiguationData":[OSD([subQ5])],"isStart":false});Q0=makeQuery(id+"F4.imprint","IMPRINT",FACE,{"disambiguationData":[TD([[makeQuery(id+"F4.imprint","IMPRINT",EDGE,{"derivedFrom":subQ6}),-1.0]])]});}
            var Q1;
            {var subQ1=sQuery(id+"F0.wireOp",EDGE,"E3.9.0.1");var subQ2=makeQuery(id+"F1.opExtrude","CAP_EDGE",EDGE,{"disambiguationData":[OSD([subQ1])],"isStart":false});Q1=makeQuery(id+"F4.imprint","IMPRINT",FACE,{"disambiguationData":[TD([[makeQuery(id+"F4.imprint","IMPRINT",EDGE,{"derivedFrom":subQ2}),-1.0]])]});}
            var Q2;
            {var subQ5=sQuery(id+"F0.wireOp",EDGE,"E29.trimOffspring");var subQ6=makeQuery(id+"F1.opExtrude","CAP_EDGE",EDGE,{"disambiguationData":[OSD([subQ5])],"isStart":false});Q2=makeQuery(id+"F4.imprint","IMPRINT",FACE,{"disambiguationData":[TD([[makeQuery(id+"F4.imprint","IMPRINT",EDGE,{"derivedFrom":subQ6}),-1.0]])]});}
            var Q3;
            {var subQ1=sQuery(id+"F0.wireOp",EDGE,"E3.7.0.1");var subQ2=makeQuery(id+"F1.opExtrude","CAP_EDGE",EDGE,{"disambiguationData":[OSD([subQ1])],"isStart":false});Q3=makeQuery(id+"F4.imprint","IMPRINT",FACE,{"disambiguationData":[TD([[makeQuery(id+"F4.imprint","IMPRINT",EDGE,{"derivedFrom":subQ2}),-1.0]])]});}
            var Q4;
            {var subQ1=sQuery(id+"F0.wireOp",EDGE,"E3.6.0.1");var subQ2=makeQuery(id+"F1.opExtrude","CAP_EDGE",EDGE,{"disambiguationData":[OSD([subQ1])],"isStart":false});Q4=makeQuery(id+"F4.imprint","IMPRINT",FACE,{"disambiguationData":[TD([[makeQuery(id+"F4.imprint","IMPRINT",EDGE,{"derivedFrom":subQ2}),-1.0]])]});}
            var Q5;
            {var subQ5=sQuery(id+"F0.wireOp",EDGE,"E14.trimOffspring");var subQ6=makeQuery(id+"F1.opExtrude","CAP_EDGE",EDGE,{"disambiguationData":[OSD([subQ5])],"isStart":false});Q5=makeQuery(id+"F4.imprint","IMPRINT",FACE,{"disambiguationData":[TD([[makeQuery(id+"F4.imprint","IMPRINT",EDGE,{"derivedFrom":subQ6}),-1.0]])]});}
            var Q6;
            {var subQ1=sQuery(id+"F0.wireOp",EDGE,"E3.4.0.1");var subQ2=makeQuery(id+"F1.opExtrude","CAP_EDGE",EDGE,{"disambiguationData":[OSD([subQ1])],"isStart":false});Q6=makeQuery(id+"F4.imprint","IMPRINT",FACE,{"disambiguationData":[TD([[makeQuery(id+"F4.imprint","IMPRINT",EDGE,{"derivedFrom":subQ2}),-1.0]])]});}
            var Q7;
            {var subQ5=sQuery(id+"F0.wireOp",EDGE,"E3.3.0.1");var subQ6=makeQuery(id+"F1.opExtrude","CAP_EDGE",EDGE,{"disambiguationData":[OSD([subQ5])],"isStart":false});Q7=makeQuery(id+"F4.imprint","IMPRINT",FACE,{"disambiguationData":[TD([[makeQuery(id+"F4.imprint","IMPRINT",EDGE,{"derivedFrom":subQ6}),-1.0]])]});}
            var Q8;
            {var subQ5=sQuery(id+"F0.wireOp",EDGE,"E18.trimOffspring");var subQ6=makeQuery(id+"F1.opExtrude","CAP_EDGE",EDGE,{"disambiguationData":[OSD([subQ5])],"isStart":false});Q8=makeQuery(id+"F4.imprint","IMPRINT",FACE,{"disambiguationData":[TD([[makeQuery(id+"F4.imprint","IMPRINT",EDGE,{"derivedFrom":subQ6}),-1.0]])]});}
            var Q9;
            {var subQ1=sQuery(id+"F0.wireOp",EDGE,"E3.1.0.1");var subQ2=makeQuery(id+"F1.opExtrude","CAP_EDGE",EDGE,{"disambiguationData":[OSD([subQ1])],"isStart":false});Q9=makeQuery(id+"F4.imprint","IMPRINT",FACE,{"disambiguationData":[TD([[makeQuery(id+"F4.imprint","IMPRINT",EDGE,{"derivedFrom":subQ2}),-1.0]])]});}
            var Q10;
            {var subQ1=sQuery(id+"F0.wireOp",EDGE,"E1");var subQ2=makeQuery(id+"F1.opExtrude","CAP_EDGE",EDGE,{"disambiguationData":[OSD([subQ1])],"isStart":false});Q10=makeQuery(id+"F4.imprint","IMPRINT",FACE,{"disambiguationData":[TD([[makeQuery(id+"F4.imprint","IMPRINT",EDGE,{"derivedFrom":subQ2}),-1.0]])]});}
            var Q11;
            {var subQ0=sQuery(id+"F4.wireOp",EDGE,"E44.left");Q11=makeQuery(id+"F4.imprint","IMPRINT",FACE,{"disambiguationData":[TD([[makeQuery(id+"F4.imprint","IMPRINT",EDGE,{"derivedFrom":subQ0}),1.0]])]});}
            var Q12;
            {var subQ6=sQuery(id+"F0.wireOp",EDGE,"E8");var subQ7=makeQuery(id+"F1.opExtrude","CAP_EDGE",EDGE,{"disambiguationData":[OSD([subQ6]),TDD([makeQuery(id+"F0.imprint","IMPRINT",EDGE,{"disambiguationData":[TD([[makeQuery(id+"F0.imprint","INTERSECT",VERTEX,{"derivedFrom":[sQuery(id+"F0.wireOp",EDGE,"E0.right"),subQ6]}),1.0]])],"derivedFrom":subQ6})])],"isStart":false});Q12=makeQuery(id+"F4.imprint","IMPRINT",FACE,{"disambiguationData":[TD([[makeQuery(id+"F4.imprint","IMPRINT",EDGE,{"derivedFrom":subQ7}),1.0]])]});}
            var Q13;
            {var subQ2=sQuery(id+"F0.wireOp",EDGE,"E24");var subQ6=sQuery(id+"F0.wireOp",EDGE,"E3.7.0.0");var subQ9=makeQuery(id+"F1.opExtrude","CAP_EDGE",EDGE,{"disambiguationData":[OSD([subQ2]),TDD([makeQuery(id+"F0.imprint","IMPRINT",EDGE,{"disambiguationData":[TD([[makeQuery(id+"F0.imprint","INTERSECT",VERTEX,{"derivedFrom":[subQ6,subQ2]}),-1.0]])],"derivedFrom":subQ2})])],"isStart":false});Q13=makeQuery(id+"F4.imprint","IMPRINT",FACE,{"disambiguationData":[TD([[makeQuery(id+"F4.imprint","IMPRINT",EDGE,{"derivedFrom":subQ9}),-1.0]])]});}
            var Q14;
            {var subQ4=sQuery(id+"F0.wireOp",EDGE,"E3.6.0.0");var subQ7=sQuery(id+"F0.wireOp",EDGE,"E24");var subQ8=makeQuery(id+"F1.opExtrude","CAP_EDGE",EDGE,{"disambiguationData":[OSD([subQ7]),TDD([makeQuery(id+"F0.imprint","IMPRINT",EDGE,{"disambiguationData":[TD([[makeQuery(id+"F0.imprint","INTERSECT",VERTEX,{"derivedFrom":[subQ4,subQ7]}),-1.0]])],"derivedFrom":subQ7})])],"isStart":false});Q14=makeQuery(id+"F4.imprint","IMPRINT",FACE,{"disambiguationData":[TD([[makeQuery(id+"F4.imprint","IMPRINT",EDGE,{"derivedFrom":subQ8}),-1.0]])]});}
            var Q15;
            {var subQ4=sQuery(id+"F0.wireOp",EDGE,"E13");var subQ5=sQuery(id+"F0.wireOp",EDGE,"E24");var subQ6=makeQuery(id+"F0.imprint","INTERSECT",VERTEX,{"derivedFrom":[subQ4,subQ5]});var subQ9=makeQuery(id+"F1.opExtrude","CAP_EDGE",EDGE,{"disambiguationData":[OSD([subQ5]),TDD([makeQuery(id+"F0.imprint","IMPRINT",EDGE,{"disambiguationData":[TD([[subQ6,-1.0]])],"derivedFrom":subQ5})])],"isStart":false});Q15=makeQuery(id+"F4.imprint","IMPRINT",FACE,{"disambiguationData":[TD([[makeQuery(id+"F4.imprint","IMPRINT",EDGE,{"derivedFrom":subQ9}),-1.0]])]});}
            var Q16;
            {var subQ2=sQuery(id+"F0.wireOp",EDGE,"E12");var subQ6=sQuery(id+"F0.wireOp",EDGE,"E3.4.0.0");var subQ9=makeQuery(id+"F1.opExtrude","CAP_EDGE",EDGE,{"disambiguationData":[OSD([subQ2]),TDD([makeQuery(id+"F0.imprint","IMPRINT",EDGE,{"disambiguationData":[TD([[makeQuery(id+"F0.imprint","INTERSECT",VERTEX,{"derivedFrom":[subQ6,subQ2]}),-1.0]])],"derivedFrom":subQ2})])],"isStart":false});Q16=makeQuery(id+"F4.imprint","IMPRINT",FACE,{"disambiguationData":[TD([[makeQuery(id+"F4.imprint","IMPRINT",EDGE,{"derivedFrom":subQ9}),-1.0]])]});}
            var Q17;
            {var subQ4=sQuery(id+"F0.wireOp",EDGE,"E3.3.0.0");var subQ7=sQuery(id+"F0.wireOp",EDGE,"E12");var subQ8=makeQuery(id+"F1.opExtrude","CAP_EDGE",EDGE,{"disambiguationData":[OSD([subQ7]),TDD([makeQuery(id+"F0.imprint","IMPRINT",EDGE,{"disambiguationData":[TD([[makeQuery(id+"F0.imprint","INTERSECT",VERTEX,{"derivedFrom":[subQ4,subQ7]}),-1.0]])],"derivedFrom":subQ7})])],"isStart":false});Q17=makeQuery(id+"F4.imprint","IMPRINT",FACE,{"disambiguationData":[TD([[makeQuery(id+"F4.imprint","IMPRINT",EDGE,{"derivedFrom":subQ8}),-1.0]])]});}
            var Q18;
            {var subQ4=sQuery(id+"F0.wireOp",EDGE,"E3.2.0.0");var subQ5=sQuery(id+"F0.wireOp",EDGE,"E12");var subQ6=makeQuery(id+"F0.imprint","INTERSECT",VERTEX,{"derivedFrom":[subQ4,subQ5]});var subQ9=makeQuery(id+"F1.opExtrude","CAP_EDGE",EDGE,{"disambiguationData":[OSD([subQ5]),TDD([makeQuery(id+"F0.imprint","IMPRINT",EDGE,{"disambiguationData":[TD([[subQ6,-1.0]])],"derivedFrom":subQ5})])],"isStart":false});Q18=makeQuery(id+"F4.imprint","IMPRINT",FACE,{"disambiguationData":[TD([[makeQuery(id+"F4.imprint","IMPRINT",EDGE,{"derivedFrom":subQ9}),-1.0]])]});}
            var Q19;
            {var subQ2=sQuery(id+"F0.wireOp",EDGE,"E8");var subQ6=sQuery(id+"F0.wireOp",EDGE,"E3.1.0.0");var subQ9=makeQuery(id+"F1.opExtrude","CAP_EDGE",EDGE,{"disambiguationData":[OSD([subQ2]),TDD([makeQuery(id+"F0.imprint","IMPRINT",EDGE,{"disambiguationData":[TD([[makeQuery(id+"F0.imprint","INTERSECT",VERTEX,{"derivedFrom":[subQ6,subQ2]}),1.0]])],"derivedFrom":subQ2})])],"isStart":false});Q19=makeQuery(id+"F4.imprint","IMPRINT",FACE,{"disambiguationData":[TD([[makeQuery(id+"F4.imprint","IMPRINT",EDGE,{"derivedFrom":subQ9}),1.0]])]});}
            var Q20;
            {var subQ4=sQuery(id+"F0.wireOp",EDGE,"E2");var subQ7=sQuery(id+"F0.wireOp",EDGE,"E8");var subQ8=makeQuery(id+"F1.opExtrude","CAP_EDGE",EDGE,{"disambiguationData":[OSD([subQ7]),TDD([makeQuery(id+"F0.imprint","IMPRINT",EDGE,{"disambiguationData":[TD([[makeQuery(id+"F0.imprint","INTERSECT",VERTEX,{"derivedFrom":[subQ4,subQ7]}),1.0]])],"derivedFrom":subQ7})])],"isStart":false});Q20=makeQuery(id+"F4.imprint","IMPRINT",FACE,{"disambiguationData":[TD([[makeQuery(id+"F4.imprint","IMPRINT",EDGE,{"derivedFrom":subQ8}),1.0]])]});}
            var Q21;
            {var subQ1=sQuery(id+"F0.wireOp",EDGE,"E1");var subQ36=makeQuery(id+"F1.opExtrude","CAP_EDGE",EDGE,{"disambiguationData":[OSD([subQ1])],"isStart":false});Q21=makeQuery(id+"F4.imprint","IMPRINT",FACE,{"disambiguationData":[TD([[makeQuery(id+"F4.imprint","IMPRINT",EDGE,{"derivedFrom":subQ36}),1.0]])]});}
            var Q22;
            {var subQ4=sQuery(id+"F0.wireOp",EDGE,"E30");var subQ5=sQuery(id+"F0.wireOp",EDGE,"E34");var subQ6=makeQuery(id+"F0.imprint","INTERSECT",VERTEX,{"derivedFrom":[subQ4,subQ5]});var subQ9=makeQuery(id+"F1.opExtrude","CAP_EDGE",EDGE,{"disambiguationData":[OSD([subQ5]),TDD([makeQuery(id+"F0.imprint","IMPRINT",EDGE,{"disambiguationData":[TD([[subQ6,-1.0]])],"derivedFrom":subQ5})])],"isStart":false});Q22=makeQuery(id+"F4.imprint","IMPRINT",FACE,{"disambiguationData":[TD([[makeQuery(id+"F4.imprint","IMPRINT",EDGE,{"derivedFrom":subQ9}),-1.0]])]});}
            var Q23;
            {var subQ4=sQuery(id+"F0.wireOp",EDGE,"E3.9.0.0");var subQ7=sQuery(id+"F0.wireOp",EDGE,"E34");var subQ8=makeQuery(id+"F1.opExtrude","CAP_EDGE",EDGE,{"disambiguationData":[OSD([subQ7]),TDD([makeQuery(id+"F0.imprint","IMPRINT",EDGE,{"disambiguationData":[TD([[makeQuery(id+"F0.imprint","INTERSECT",VERTEX,{"derivedFrom":[subQ4,subQ7]}),-1.0]])],"derivedFrom":subQ7})])],"isStart":false});Q23=makeQuery(id+"F4.imprint","IMPRINT",FACE,{"disambiguationData":[TD([[makeQuery(id+"F4.imprint","IMPRINT",EDGE,{"derivedFrom":subQ8}),-1.0]])]});}
            var Q24;
            {var subQ2=sQuery(id+"F0.wireOp",EDGE,"E34");var subQ6=sQuery(id+"F0.wireOp",EDGE,"E3.10.0.0");var subQ9=makeQuery(id+"F1.opExtrude","CAP_EDGE",EDGE,{"disambiguationData":[OSD([subQ2]),TDD([makeQuery(id+"F0.imprint","IMPRINT",EDGE,{"disambiguationData":[TD([[makeQuery(id+"F0.imprint","INTERSECT",VERTEX,{"derivedFrom":[subQ6,subQ2]}),-1.0]])],"derivedFrom":subQ2})])],"isStart":false});Q24=makeQuery(id+"F4.imprint","IMPRINT",FACE,{"disambiguationData":[TD([[makeQuery(id+"F4.imprint","IMPRINT",EDGE,{"derivedFrom":subQ9}),-1.0]])]});}
            var Q25;
            {var subQ5=sQuery(id+"F0.wireOp",EDGE,"E38.trimOffspring");var subQ6=makeQuery(id+"F1.opExtrude","CAP_EDGE",EDGE,{"disambiguationData":[OSD([subQ5])],"isStart":false});Q25=makeQuery(id+"F4.imprint","IMPRINT",FACE,{"disambiguationData":[TD([[makeQuery(id+"F4.imprint","IMPRINT",EDGE,{"derivedFrom":subQ6}),-1.0]])]});}
            extrude(context, id + "F5", {"entities" : qUnion([Q0, Q1, Q2, Q3, Q4, Q5, Q6, Q7, Q8, Q9, Q10, Q11, Q12, Q13, Q14, Q15, Q16, Q17, Q18, Q19, Q20, Q21, Q22, Q23, Q24, Q25]), "operationType" : NewBodyOperationType.ADD, "depth" : 12 * mm});
        }
        {
            var Q0;
            {var subQ0=sQuery(id+"F0.wireOp",EDGE,"E0.bottom");var subQ1=makeQuery(id+"F0.imprint","INTERSECT",VERTEX,{"derivedFrom":[subQ0,sQuery(id+"F0.wireOp",EDGE,"E3.2.0.1")]});var subQ2=makeQuery(id+"F0.imprint","INTERSECT",VERTEX,{"derivedFrom":[subQ0,sQuery(id+"F0.wireOp",EDGE,"E3.5.0.0")]});var subQ3=makeQuery(id+"F0.imprint","INTERSECT",VERTEX,{"derivedFrom":[subQ0,sQuery(id+"F0.wireOp",EDGE,"E3.8.0.0")]});Q0=makeQuery(id+"F3.boolean.opBoolean","MERGE",FACE,{"derivedFrom":[makeQuery(id+"F1.opExtrude","SWEPT_FACE",FACE,{"disambiguationData":[OSD([subQ0]),TDD([makeQuery(id+"F0.imprint","IMPRINT",EDGE,{"disambiguationData":[TD([[makeQuery(id+"F0.imprint","INTERSECT",VERTEX,{"derivedFrom":[subQ0,sQuery(id+"F0.wireOp",EDGE,"E3.11.0.0")]}),-1.0]])],"derivedFrom":subQ0})])]}),makeQuery(id+"F1.opExtrude","SWEPT_FACE",FACE,{"disambiguationData":[OSD([subQ0]),TDD([makeQuery(id+"F0.imprint","IMPRINT",EDGE,{"disambiguationData":[TD([[makeQuery(id+"F0.imprint","INTERSECT",VERTEX,{"derivedFrom":[subQ0,sQuery(id+"F0.wireOp",EDGE,"E3.10.0.0")]}),-1.0]])],"derivedFrom":subQ0})])]}),makeQuery(id+"F1.opExtrude","SWEPT_FACE",FACE,{"disambiguationData":[OSD([subQ0]),TDD([makeQuery(id+"F0.imprint","IMPRINT",EDGE,{"disambiguationData":[TD([[makeQuery(id+"F0.imprint","INTERSECT",VERTEX,{"derivedFrom":[subQ0,sQuery(id+"F0.wireOp",EDGE,"E3.9.0.0")]}),-1.0]])],"derivedFrom":subQ0})])]}),makeQuery(id+"F1.opExtrude","SWEPT_FACE",FACE,{"disambiguationData":[OSD([subQ0]),TDD([makeQuery(id+"F0.imprint","IMPRINT",EDGE,{"disambiguationData":[TD([[subQ3,1.0]])],"derivedFrom":subQ0}),makeQuery(id+"F0.imprint","IMPRINT",EDGE,{"disambiguationData":[TD([[subQ3,-1.0]])],"derivedFrom":subQ0})])]}),makeQuery(id+"F1.opExtrude","SWEPT_FACE",FACE,{"disambiguationData":[OSD([subQ0]),TDD([makeQuery(id+"F0.imprint","IMPRINT",EDGE,{"disambiguationData":[TD([[makeQuery(id+"F0.imprint","INTERSECT",VERTEX,{"derivedFrom":[subQ0,sQuery(id+"F0.wireOp",EDGE,"E3.7.0.0")]}),-1.0]])],"derivedFrom":subQ0})])]}),makeQuery(id+"F1.opExtrude","SWEPT_FACE",FACE,{"disambiguationData":[OSD([subQ0]),TDD([makeQuery(id+"F0.imprint","IMPRINT",EDGE,{"disambiguationData":[TD([[makeQuery(id+"F0.imprint","INTERSECT",VERTEX,{"derivedFrom":[subQ0,sQuery(id+"F0.wireOp",EDGE,"E3.6.0.0")]}),-1.0]])],"derivedFrom":subQ0})])]}),makeQuery(id+"F1.opExtrude","SWEPT_FACE",FACE,{"disambiguationData":[OSD([subQ0]),TDD([makeQuery(id+"F0.imprint","IMPRINT",EDGE,{"disambiguationData":[TD([[subQ2,1.0]])],"derivedFrom":subQ0}),makeQuery(id+"F0.imprint","IMPRINT",EDGE,{"disambiguationData":[TD([[subQ2,-1.0]])],"derivedFrom":subQ0})])]}),makeQuery(id+"F1.opExtrude","SWEPT_FACE",FACE,{"disambiguationData":[OSD([subQ0]),TDD([makeQuery(id+"F0.imprint","IMPRINT",EDGE,{"disambiguationData":[TD([[makeQuery(id+"F0.imprint","INTERSECT",VERTEX,{"derivedFrom":[subQ0,sQuery(id+"F0.wireOp",EDGE,"E3.4.0.0")]}),-1.0]])],"derivedFrom":subQ0})])]}),makeQuery(id+"F1.opExtrude","SWEPT_FACE",FACE,{"disambiguationData":[OSD([subQ0]),TDD([makeQuery(id+"F0.imprint","IMPRINT",EDGE,{"disambiguationData":[TD([[makeQuery(id+"F0.imprint","INTERSECT",VERTEX,{"derivedFrom":[subQ0,sQuery(id+"F0.wireOp",EDGE,"E3.3.0.0")]}),-1.0]])],"derivedFrom":subQ0})])]}),makeQuery(id+"F1.opExtrude","SWEPT_FACE",FACE,{"disambiguationData":[OSD([subQ0]),TDD([makeQuery(id+"F0.imprint","IMPRINT",EDGE,{"disambiguationData":[TD([[makeQuery(id+"F0.imprint","INTERSECT",VERTEX,{"derivedFrom":[subQ0,sQuery(id+"F0.wireOp",EDGE,"E3.2.0.0")]}),-1.0]])],"derivedFrom":subQ0}),makeQuery(id+"F0.imprint","IMPRINT",EDGE,{"disambiguationData":[TD([[subQ1,-1.0]])],"derivedFrom":subQ0})])]}),makeQuery(id+"F1.opExtrude","SWEPT_FACE",FACE,{"disambiguationData":[OSD([subQ0]),TDD([makeQuery(id+"F0.imprint","IMPRINT",EDGE,{"disambiguationData":[TD([[makeQuery(id+"F0.imprint","INTERSECT",VERTEX,{"derivedFrom":[subQ0,sQuery(id+"F0.wireOp",EDGE,"E3.1.0.0")]}),-1.0]])],"derivedFrom":subQ0})])]}),makeQuery(id+"F1.opExtrude","SWEPT_FACE",FACE,{"disambiguationData":[OSD([subQ0]),TDD([makeQuery(id+"F0.imprint","IMPRINT",EDGE,{"disambiguationData":[TD([[makeQuery(id+"F0.imprint","INTERSECT",VERTEX,{"derivedFrom":[subQ0,sQuery(id+"F0.wireOp",EDGE,"E2")]}),-1.0]])],"derivedFrom":subQ0})])]}),makeQuery(id+"F3.opExtrude","SWEPT_FACE",FACE,{"disambiguationData":[OSD([sQuery(id+"F2.wireOp",EDGE,"E39.bottom")])]})]});}
            var sketch = newSketch(context, id + "F6", { "sketchPlane" : qUnion([Q0])});
            skLineSegment(sketch, "E45.bottom", {"start": v(0, 0) * mm, "end": v(400, 0) * mm});
            skLineSegment(sketch, "E45.top", {"start": v(0, 7400) * mm, "end": v(400, 7400) * mm});
            skLineSegment(sketch, "E45.left", {"start": v(0, 0) * mm, "end": v(0, 7400) * mm});
            skLineSegment(sketch, "E45.right", {"start": v(400, 0) * mm, "end": v(400, 7400) * mm});
            skSolve(sketch);
        }
        {
            var Q0;
            Q0 = qSketchRegion(id + "F6", true);
            var Q1;
            {var subQ22=sQuery(id+"F2.wireOp",EDGE,"E39.bottom");Q1=makeQuery(id+"F6.imprint","IMPRINT",FACE,{"disambiguationData":[TD([[makeQuery(id+"F6.imprint","IMPRINT",EDGE,{"derivedFrom":makeQuery(id+"F3.opExtrude","CAP_EDGE",EDGE,{"disambiguationData":[OSD([subQ22])],"isStart":false})}),-1.0]])]});}
            extrude(context, id + "F7", {"entities" : qUnion([Q0, Q1]), "operationType" : NewBodyOperationType.ADD, "depth" : 12 * mm});
        }
        {
            var Q0;
            {var subQ0=sQuery(id+"F2.wireOp",EDGE,"E39.left");Q0=makeQuery(id+"F7.boolean.opBoolean","MERGE",FACE,{"derivedFrom":[makeQuery(id+"F3.opExtrude","SWEPT_FACE",FACE,{"disambiguationData":[OSD([subQ0])]}),makeQuery(id+"F7.opExtrude","SWEPT_FACE",FACE,{"disambiguationData":[OSD([sQuery(id+"F2.wireOp",EDGE,"E39.bottom"),subQ0,sQuery(id+"F6.wireOp",EDGE,"E45.bottom")])]})]});}
            var sketch = newSketch(context, id + "F8", { "sketchPlane" : qUnion([Q0])});
            skLineSegment(sketch, "E46", {"start": v(0, 2900) * mm, "end": v(-450, 3277.6) * mm});
            skLineSegment(sketch, "E47", {"start": v(-450, 3277.6) * mm, "end": v(-450, 3377.6) * mm});
            skLineSegment(sketch, "E48", {"start": v(-450, 3377.6) * mm, "end": v(50, 3377.6) * mm});
            skLineSegment(sketch, "E49", {"start": v(50, 3377.6) * mm, "end": v(50, 2858.05) * mm});
            skLineSegment(sketch, "E50", {"start": v(0, 2900) * mm, "end": v(50, 2858.05) * mm});
            skSolve(sketch);
        }
        {
            var Q0;
            Q0 = qSketchRegion(id + "F8", true);
            extrude(context, id + "F9", {"entities" : qUnion([Q0]), "operationType" : NewBodyOperationType.REMOVE, "endBound" : BoundingType.THROUGH_ALL, "oppositeDirection" : true, "depth" : 25 * mm});
        }
    });
